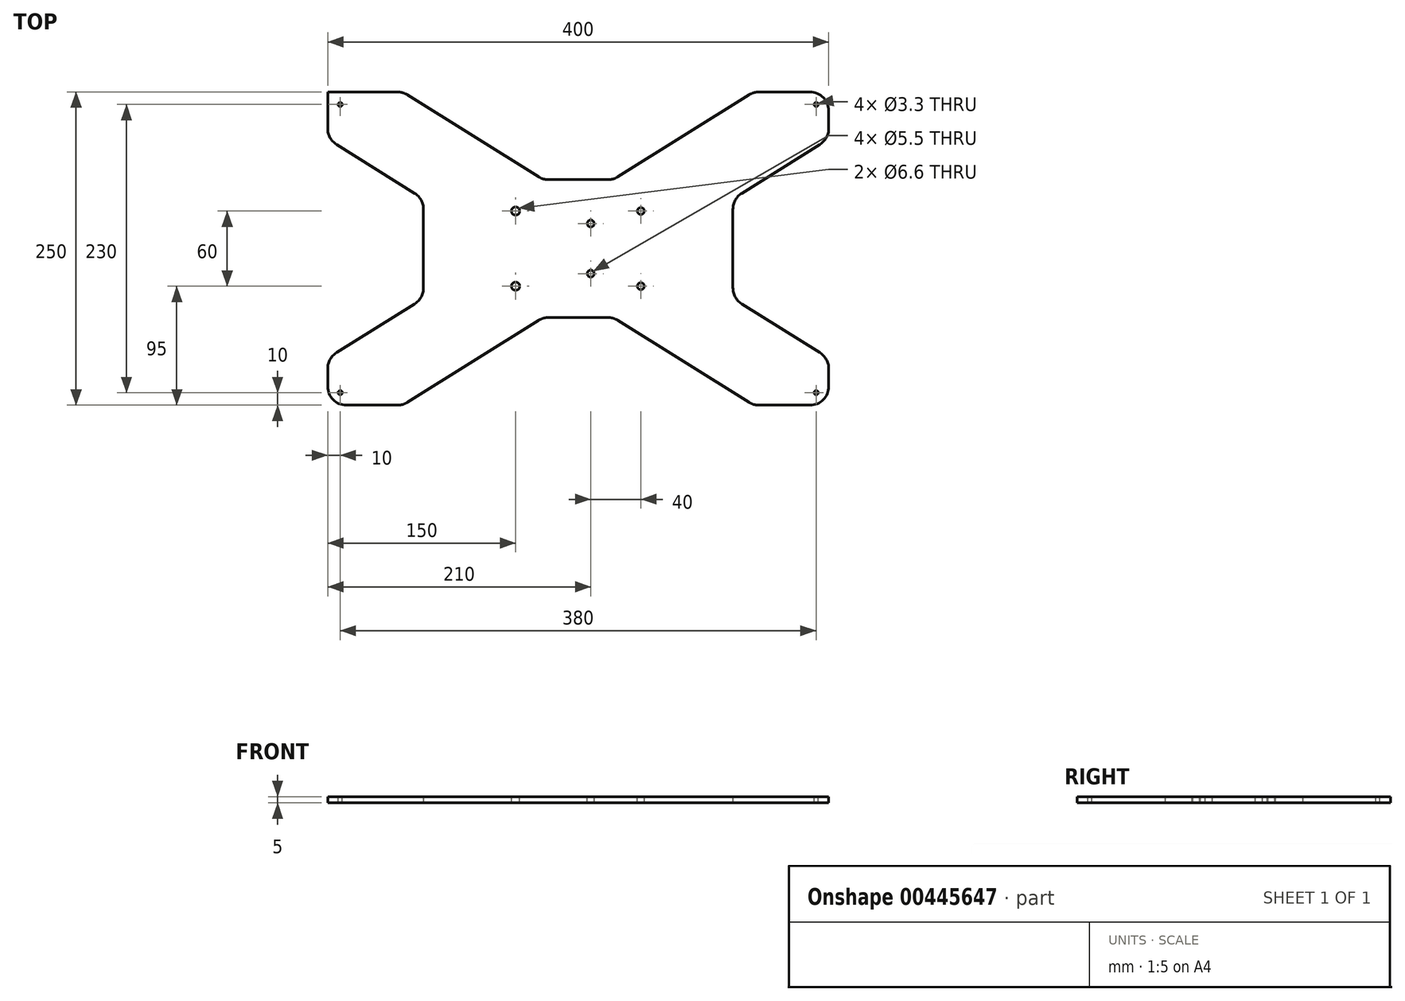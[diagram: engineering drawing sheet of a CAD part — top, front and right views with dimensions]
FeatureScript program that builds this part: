
annotation { "Feature Type Name" : "Feature", "Feature Type Description" : "" }
export const myFeature = defineFeature(function(context is Context, id is Id, definition is map)
    precondition{}
    {
        {
            var Q0;
            Q0=qCreatedBy(makeId("Top.planeOp"),FACE);
            var sketch = newSketch(context, id + "F0", { "sketchPlane" : qUnion([Q0])});
            skLineSegment(sketch, "E0.bottom", {"start": v(200, -125) * mm, "end": v(140, -125) * mm});
            skLineSegment(sketch, "E0.top", {"start": v(200, 125) * mm, "end": v(140, 125) * mm});
            skLineSegment(sketch, "E0.left", {"start": v(200, -125) * mm, "end": v(200, -87.5) * mm});
            skLineSegment(sketch, "E0.right", {"start": v(-200, -125) * mm, "end": v(-200, -87.5) * mm});
            skPoint(sketch, "E0.middle", {"position": v(0, 0) * mm});
            skLineSegment(sketch, "E1.bottom", {"start": v(-28, -55) * mm, "end": v(28, -55) * mm});
            skLineSegment(sketch, "E1.left", {"start": v(-123.5, -39.69) * mm, "end": v(-123.5, 39.69) * mm});
            skLineSegment(sketch, "E1.right", {"start": v(123.5, -39.69) * mm, "end": v(123.5, 39.69) * mm});
            skLineSegment(sketch, "E2", {"start": v(-200, -125) * mm, "end": v(200, 125) * mm, "construction": true});
            skLineSegment(sketch, "E3", {"start": v(-200, 125) * mm, "end": v(200, -125) * mm, "construction": true});
            skLineSegment(sketch, "E4.bottom", {"start": v(-200, -125) * mm, "end": v(-140, -125) * mm});
            skLineSegment(sketch, "E5.MirrorCS", {"start": v(-200, 125) * mm, "end": v(-140, 125) * mm});
            skLineSegment(sketch, "E6.MirrorCS", {"start": v(-200, 125) * mm, "end": v(-200, 87.5) * mm});
            skLineSegment(sketch, "E7", {"start": v(-200, 87.5) * mm, "end": v(-123.5, 39.69) * mm});
            skLineSegment(sketch, "E8", {"start": v(-140, 125) * mm, "end": v(-28, 55) * mm});
            skLineSegment(sketch, "E9", {"start": v(-200, -87.5) * mm, "end": v(-123.5, -39.69) * mm});
            skLineSegment(sketch, "E10", {"start": v(-140, -125) * mm, "end": v(-28, -55) * mm});
            skPoint(sketch, "E11.MirrorCS.end.orphan", {"position": v(-140, 87.5) * mm});
            skPoint(sketch, "E12.MirrorCS.end.orphan", {"position": v(140, 87.5) * mm});
            skPoint(sketch, "E4.top.end.orphan", {"position": v(-140, -87.5) * mm});
            skPoint(sketch, "E13.MirrorCS.end.orphan", {"position": v(140, -87.5) * mm});
            skLineSegment(sketch, "E14.trimOffspring", {"start": v(123.5, 39.69) * mm, "end": v(200, 87.5) * mm});
            skLineSegment(sketch, "E15.trimOffspring", {"start": v(123.5, -39.69) * mm, "end": v(200, -87.5) * mm});
            skLineSegment(sketch, "E16.trimOffspring", {"start": v(28, 55) * mm, "end": v(140, 125) * mm});
            skLineSegment(sketch, "E17.trimOffspring", {"start": v(28, -55) * mm, "end": v(140, -125) * mm});
            skLineSegment(sketch, "E18.trimOffspring", {"start": v(-200, 87.5) * mm, "end": v(-200, 125) * mm});
            skLineSegment(sketch, "E19.trimOffspring", {"start": v(-140, 125) * mm, "end": v(-200, 125) * mm});
            skLineSegment(sketch, "E20.trimOffspring", {"start": v(200, 87.5) * mm, "end": v(200, 125) * mm});
            skLineSegment(sketch, "E21.trimOffspring", {"start": v(-140, -125) * mm, "end": v(-200, -125) * mm});
            skPoint(sketch, "E22.orphan", {"position": v(123.5, 55) * mm});
            skLineSegment(sketch, "E23.trimOffspring", {"start": v(-28, 55) * mm, "end": v(28, 55) * mm});
            skPoint(sketch, "E24.orphan", {"position": v(-123.5, 55) * mm});
            skPoint(sketch, "E25.orphan", {"position": v(-123.5, -55) * mm});
            skPoint(sketch, "E26.orphan", {"position": v(123.5, -55) * mm});
            skSolve(sketch);
        }
        {
            var Q0;
            Q0=qSketchRegion(id+"F0",true);
            extrude(context, id + "F1", {"entities" : qUnion([Q0]), "depth" : 5 * mm});
        }
        {
            var Q0;
            Q0=makeQuery(id+"F1.opExtrude","CAP_FACE",FACE,{"disambiguationData":[OSD([sQuery(id+"F0.wireOp",EDGE,"E1.bottom"),sQuery(id+"F0.wireOp",EDGE,"E1.left"),sQuery(id+"F0.wireOp",EDGE,"E1.right"),sQuery(id+"F0.wireOp",EDGE,"E0.right"),sQuery(id+"F0.wireOp",EDGE,"E0.top"),sQuery(id+"F0.wireOp",EDGE,"E0.left"),sQuery(id+"F0.wireOp",EDGE,"E0.bottom"),sQuery(id+"F0.wireOp",EDGE,"E7"),sQuery(id+"F0.wireOp",EDGE,"E8"),sQuery(id+"F0.wireOp",EDGE,"E9"),sQuery(id+"F0.wireOp",EDGE,"E10"),sQuery(id+"F0.wireOp",EDGE,"E14.trimOffspring"),sQuery(id+"F0.wireOp",EDGE,"E15.trimOffspring"),sQuery(id+"F0.wireOp",EDGE,"E16.trimOffspring"),sQuery(id+"F0.wireOp",EDGE,"E17.trimOffspring"),sQuery(id+"F0.wireOp",EDGE,"E18.trimOffspring"),sQuery(id+"F0.wireOp",EDGE,"E19.trimOffspring"),sQuery(id+"F0.wireOp",EDGE,"E21.trimOffspring"),sQuery(id+"F0.wireOp",EDGE,"E20.trimOffspring"),sQuery(id+"F0.wireOp",EDGE,"E23.trimOffspring")])],"isStart":false});
            var sketch = newSketch(context, id + "F2", { "sketchPlane" : qUnion([Q0])});
            skPoint(sketch, "E27", {"position": v(-190, 115) * mm});
            skPoint(sketch, "E28.0.1.0", {"position": v(-190, -115) * mm});
            skPoint(sketch, "E28.1.0.0", {"position": v(190, 115) * mm});
            skPoint(sketch, "E28.1.1.0", {"position": v(190, -115) * mm});
            skLineSegment(sketch, "E28.direction1", {"start": v(-190, 115) * mm, "end": v(190, 115) * mm, "construction": true});
            skLineSegment(sketch, "E28.direction2", {"start": v(-190, 115) * mm, "end": v(-190, -115) * mm, "construction": true});
            skLineSegment(sketch, "E29.bottom", {"start": v(-50, -30) * mm, "end": v(50, -30) * mm, "construction": true});
            skLineSegment(sketch, "E29.top", {"start": v(-50, 30) * mm, "end": v(50, 30) * mm, "construction": true});
            skLineSegment(sketch, "E29.left", {"start": v(-50, -30) * mm, "end": v(-50, 30) * mm, "construction": true});
            skLineSegment(sketch, "E29.right", {"start": v(50, -30) * mm, "end": v(50, 30) * mm, "construction": true});
            skPoint(sketch, "E29.middle", {"position": v(0, 0) * mm});
            skPoint(sketch, "E30", {"position": v(-50, 30) * mm});
            skPoint(sketch, "E31", {"position": v(-50, -30) * mm});
            skPoint(sketch, "E32", {"position": v(50, 30) * mm});
            skPoint(sketch, "E33", {"position": v(50, -30) * mm});
            skPoint(sketch, "E34", {"position": v(10, -20) * mm});
            skPoint(sketch, "E35", {"position": v(10, 20) * mm});
            skSolve(sketch);
        }
        {
            var Q0;
            Q0=sQuery(id+"F2.wireOp",VERTEX,"E27");
            var Q1;
            Q1=sQuery(id+"F2.wireOp",VERTEX,"E28.0.1.0");
            var Q2;
            Q2=sQuery(id+"F2.wireOp",VERTEX,"E28.1.1.0");
            var Q3;
            Q3=sQuery(id+"F2.wireOp",VERTEX,"E28.1.0.0");
            var Q4;
            Q4=makeQuery(id+"F1.opExtrude","SWEPT_BODY",BODY,{"disambiguationData":[OSD([sQuery(id+"F0.wireOp",EDGE,"E1.bottom"),sQuery(id+"F0.wireOp",EDGE,"E1.left"),sQuery(id+"F0.wireOp",EDGE,"E1.right"),sQuery(id+"F0.wireOp",EDGE,"E0.right"),sQuery(id+"F0.wireOp",EDGE,"E0.top"),sQuery(id+"F0.wireOp",EDGE,"E0.left"),sQuery(id+"F0.wireOp",EDGE,"E0.bottom"),sQuery(id+"F0.wireOp",EDGE,"E7"),sQuery(id+"F0.wireOp",EDGE,"E8"),sQuery(id+"F0.wireOp",EDGE,"E9"),sQuery(id+"F0.wireOp",EDGE,"E10"),sQuery(id+"F0.wireOp",EDGE,"E14.trimOffspring"),sQuery(id+"F0.wireOp",EDGE,"E15.trimOffspring"),sQuery(id+"F0.wireOp",EDGE,"E16.trimOffspring"),sQuery(id+"F0.wireOp",EDGE,"E17.trimOffspring"),sQuery(id+"F0.wireOp",EDGE,"E18.trimOffspring"),sQuery(id+"F0.wireOp",EDGE,"E19.trimOffspring"),sQuery(id+"F0.wireOp",EDGE,"E21.trimOffspring"),sQuery(id+"F0.wireOp",EDGE,"E20.trimOffspring"),sQuery(id+"F0.wireOp",EDGE,"E23.trimOffspring")])]});
            hole(context, id + "F3", {"style" : HoleStyle.SIMPLE, "endStyle" : HoleEndStyle.BLIND, "standardTappedOrClearance" : lookupTablePath({ "standard" : "ISO", "fit" : "Normal", "size" : "M3", "type" : "Clearance" }), "standardBlindInLast" : lookupTablePath({ "fit" : "Standard", "standard" : "ISO", "size" : "M3", "type" : "Clearance" }), "holeDiameter" : 3.3 * mm, "holeDepth" : 13.8 * mm, "tappedDepth" : 12 * mm, "tapClearance" : 3, "locations" : qUnion([Q0, Q1, Q2, Q3]), "scope" : qUnion([Q4])});
        }
        {
            var Q0;
            Q0=sQuery(id+"F2.wireOp",VERTEX,"E33");
            var Q1;
            Q1=sQuery(id+"F2.wireOp",VERTEX,"E32");
            var Q2;
            Q2=sQuery(id+"F2.wireOp",VERTEX,"E35");
            var Q3;
            Q3=sQuery(id+"F2.wireOp",VERTEX,"E34");
            var Q4;
            Q4=makeQuery(id+"F1.opExtrude","SWEPT_BODY",BODY,{"disambiguationData":[OSD([sQuery(id+"F0.wireOp",EDGE,"E1.bottom"),sQuery(id+"F0.wireOp",EDGE,"E1.left"),sQuery(id+"F0.wireOp",EDGE,"E1.right"),sQuery(id+"F0.wireOp",EDGE,"E0.right"),sQuery(id+"F0.wireOp",EDGE,"E0.top"),sQuery(id+"F0.wireOp",EDGE,"E0.left"),sQuery(id+"F0.wireOp",EDGE,"E0.bottom"),sQuery(id+"F0.wireOp",EDGE,"E7"),sQuery(id+"F0.wireOp",EDGE,"E8"),sQuery(id+"F0.wireOp",EDGE,"E9"),sQuery(id+"F0.wireOp",EDGE,"E10"),sQuery(id+"F0.wireOp",EDGE,"E14.trimOffspring"),sQuery(id+"F0.wireOp",EDGE,"E15.trimOffspring"),sQuery(id+"F0.wireOp",EDGE,"E16.trimOffspring"),sQuery(id+"F0.wireOp",EDGE,"E17.trimOffspring"),sQuery(id+"F0.wireOp",EDGE,"E18.trimOffspring"),sQuery(id+"F0.wireOp",EDGE,"E19.trimOffspring"),sQuery(id+"F0.wireOp",EDGE,"E21.trimOffspring"),sQuery(id+"F0.wireOp",EDGE,"E20.trimOffspring"),sQuery(id+"F0.wireOp",EDGE,"E23.trimOffspring")])]});
            hole(context, id + "F4", {"style" : HoleStyle.SIMPLE, "endStyle" : HoleEndStyle.BLIND, "standardTappedOrClearance" : lookupTablePath({ "standard" : "ISO", "fit" : "Normal", "size" : "M5", "type" : "Clearance" }), "standardBlindInLast" : lookupTablePath({ "fit" : "Standard", "standard" : "ISO", "size" : "M5", "type" : "Clearance" }), "holeDiameter" : 5.5 * mm, "holeDepth" : 13.8 * mm, "tappedDepth" : 12 * mm, "tapClearance" : 3, "locations" : qUnion([Q0, Q1, Q2, Q3]), "scope" : qUnion([Q4])});
        }
        {
            var Q0;
            Q0=sQuery(id+"F2.wireOp",VERTEX,"E30");
            var Q1;
            Q1=sQuery(id+"F2.wireOp",VERTEX,"E31");
            var Q2;
            Q2=makeQuery(id+"F1.opExtrude","SWEPT_BODY",BODY,{"disambiguationData":[OSD([sQuery(id+"F0.wireOp",EDGE,"E1.bottom"),sQuery(id+"F0.wireOp",EDGE,"E1.left"),sQuery(id+"F0.wireOp",EDGE,"E1.right"),sQuery(id+"F0.wireOp",EDGE,"E0.right"),sQuery(id+"F0.wireOp",EDGE,"E0.top"),sQuery(id+"F0.wireOp",EDGE,"E0.left"),sQuery(id+"F0.wireOp",EDGE,"E0.bottom"),sQuery(id+"F0.wireOp",EDGE,"E7"),sQuery(id+"F0.wireOp",EDGE,"E8"),sQuery(id+"F0.wireOp",EDGE,"E9"),sQuery(id+"F0.wireOp",EDGE,"E10"),sQuery(id+"F0.wireOp",EDGE,"E14.trimOffspring"),sQuery(id+"F0.wireOp",EDGE,"E15.trimOffspring"),sQuery(id+"F0.wireOp",EDGE,"E16.trimOffspring"),sQuery(id+"F0.wireOp",EDGE,"E17.trimOffspring"),sQuery(id+"F0.wireOp",EDGE,"E18.trimOffspring"),sQuery(id+"F0.wireOp",EDGE,"E19.trimOffspring"),sQuery(id+"F0.wireOp",EDGE,"E21.trimOffspring"),sQuery(id+"F0.wireOp",EDGE,"E20.trimOffspring"),sQuery(id+"F0.wireOp",EDGE,"E23.trimOffspring")])]});
            hole(context, id + "F5", {"style" : HoleStyle.SIMPLE, "endStyle" : HoleEndStyle.BLIND, "standardTappedOrClearance" : lookupTablePath({ "standard" : "ISO", "fit" : "Normal", "size" : "M6", "type" : "Clearance" }), "standardBlindInLast" : lookupTablePath({ "fit" : "Standard", "standard" : "ISO", "size" : "M6", "type" : "Clearance" }), "holeDiameter" : 6.6 * mm, "holeDepth" : 13.8 * mm, "tappedDepth" : 12 * mm, "tapClearance" : 3, "locations" : qUnion([Q0, Q1]), "scope" : qUnion([Q2])});
        }
        {
            var Q0;
            Q0=makeQuery(id+"F1.opExtrude","SWEPT_EDGE",EDGE,{"disambiguationData":[OSD([sQuery(id+"F0.wireOp",EDGE,"E1.bottom"),sQuery(id+"F0.wireOp",EDGE,"E10")])]});
            var Q1;
            Q1=makeQuery(id+"F1.opExtrude","SWEPT_EDGE",EDGE,{"disambiguationData":[OSD([sQuery(id+"F0.wireOp",EDGE,"E1.bottom"),sQuery(id+"F0.wireOp",EDGE,"E17.trimOffspring")])]});
            var Q2;
            Q2=makeQuery(id+"F1.opExtrude","SWEPT_EDGE",EDGE,{"disambiguationData":[OSD([sQuery(id+"F0.wireOp",EDGE,"E0.bottom"),sQuery(id+"F0.wireOp",EDGE,"E17.trimOffspring")])]});
            var Q3;
            Q3=makeQuery(id+"F1.opExtrude","SWEPT_EDGE",EDGE,{"disambiguationData":[OSD([sQuery(id+"F0.wireOp",EDGE,"E0.left"),sQuery(id+"F0.wireOp",EDGE,"E0.bottom")])]});
            var Q4;
            Q4=makeQuery(id+"F1.opExtrude","SWEPT_EDGE",EDGE,{"disambiguationData":[OSD([sQuery(id+"F0.wireOp",EDGE,"E0.left"),sQuery(id+"F0.wireOp",EDGE,"E15.trimOffspring")])]});
            var Q5;
            Q5=makeQuery(id+"F1.opExtrude","SWEPT_EDGE",EDGE,{"disambiguationData":[OSD([sQuery(id+"F0.wireOp",EDGE,"E1.right"),sQuery(id+"F0.wireOp",EDGE,"E15.trimOffspring")])]});
            var Q6;
            Q6=makeQuery(id+"F1.opExtrude","SWEPT_EDGE",EDGE,{"disambiguationData":[OSD([sQuery(id+"F0.wireOp",EDGE,"E1.right"),sQuery(id+"F0.wireOp",EDGE,"E14.trimOffspring")])]});
            var Q7;
            Q7=makeQuery(id+"F1.opExtrude","SWEPT_EDGE",EDGE,{"disambiguationData":[OSD([sQuery(id+"F0.wireOp",EDGE,"E14.trimOffspring"),sQuery(id+"F0.wireOp",EDGE,"E20.trimOffspring")])]});
            var Q8;
            Q8=makeQuery(id+"F1.opExtrude","SWEPT_EDGE",EDGE,{"disambiguationData":[OSD([sQuery(id+"F0.wireOp",EDGE,"E0.top"),sQuery(id+"F0.wireOp",EDGE,"E20.trimOffspring")])]});
            var Q9;
            Q9=makeQuery(id+"F1.opExtrude","SWEPT_EDGE",EDGE,{"disambiguationData":[OSD([sQuery(id+"F0.wireOp",EDGE,"E0.top"),sQuery(id+"F0.wireOp",EDGE,"E16.trimOffspring")])]});
            var Q10;
            Q10=makeQuery(id+"F1.opExtrude","SWEPT_EDGE",EDGE,{"disambiguationData":[OSD([sQuery(id+"F0.wireOp",EDGE,"E16.trimOffspring"),sQuery(id+"F0.wireOp",EDGE,"E23.trimOffspring")])]});
            var Q11;
            Q11=makeQuery(id+"F1.opExtrude","SWEPT_EDGE",EDGE,{"disambiguationData":[OSD([sQuery(id+"F0.wireOp",EDGE,"E8"),sQuery(id+"F0.wireOp",EDGE,"E23.trimOffspring")])]});
            var Q12;
            Q12=makeQuery(id+"F1.opExtrude","SWEPT_EDGE",EDGE,{"disambiguationData":[OSD([sQuery(id+"F0.wireOp",EDGE,"E8"),sQuery(id+"F0.wireOp",EDGE,"E19.trimOffspring")])]});
            var Q13;
            Q13=makeQuery(id+"F1.opExtrude","SWEPT_EDGE",EDGE,{"disambiguationData":[OSD([sQuery(id+"F0.wireOp",EDGE,"E18.trimOffspring"),sQuery(id+"F0.wireOp",EDGE,"E19.trimOffspring")])]});
            var Q14;
            Q14=makeQuery(id+"F1.opExtrude","SWEPT_EDGE",EDGE,{"disambiguationData":[OSD([sQuery(id+"F0.wireOp",EDGE,"E7"),sQuery(id+"F0.wireOp",EDGE,"E18.trimOffspring")])]});
            var Q15;
            Q15=makeQuery(id+"F1.opExtrude","SWEPT_EDGE",EDGE,{"disambiguationData":[OSD([sQuery(id+"F0.wireOp",EDGE,"E1.left"),sQuery(id+"F0.wireOp",EDGE,"E7")])]});
            var Q16;
            Q16=makeQuery(id+"F1.opExtrude","SWEPT_EDGE",EDGE,{"disambiguationData":[OSD([sQuery(id+"F0.wireOp",EDGE,"E1.left"),sQuery(id+"F0.wireOp",EDGE,"E9")])]});
            var Q17;
            Q17=makeQuery(id+"F1.opExtrude","SWEPT_EDGE",EDGE,{"disambiguationData":[OSD([sQuery(id+"F0.wireOp",EDGE,"E0.right"),sQuery(id+"F0.wireOp",EDGE,"E9")])]});
            var Q18;
            Q18=makeQuery(id+"F1.opExtrude","SWEPT_EDGE",EDGE,{"disambiguationData":[OSD([sQuery(id+"F0.wireOp",EDGE,"E0.right"),sQuery(id+"F0.wireOp",EDGE,"E21.trimOffspring")])]});
            var Q19;
            Q19=makeQuery(id+"F1.opExtrude","SWEPT_EDGE",EDGE,{"disambiguationData":[OSD([sQuery(id+"F0.wireOp",EDGE,"E10"),sQuery(id+"F0.wireOp",EDGE,"E21.trimOffspring")])]});
            fillet(context, id + "F6", {"entities" : qUnion([Q0, Q1, Q2, Q3, Q4, Q5, Q6, Q7, Q8, Q9, Q10, Q11, Q12, Q13, Q14, Q15, Q16, Q17, Q18, Q19]), "radius" : 15 * mm, "tangentPropagation" : true, "allowEdgeOverflow" : false});
        }
    });
